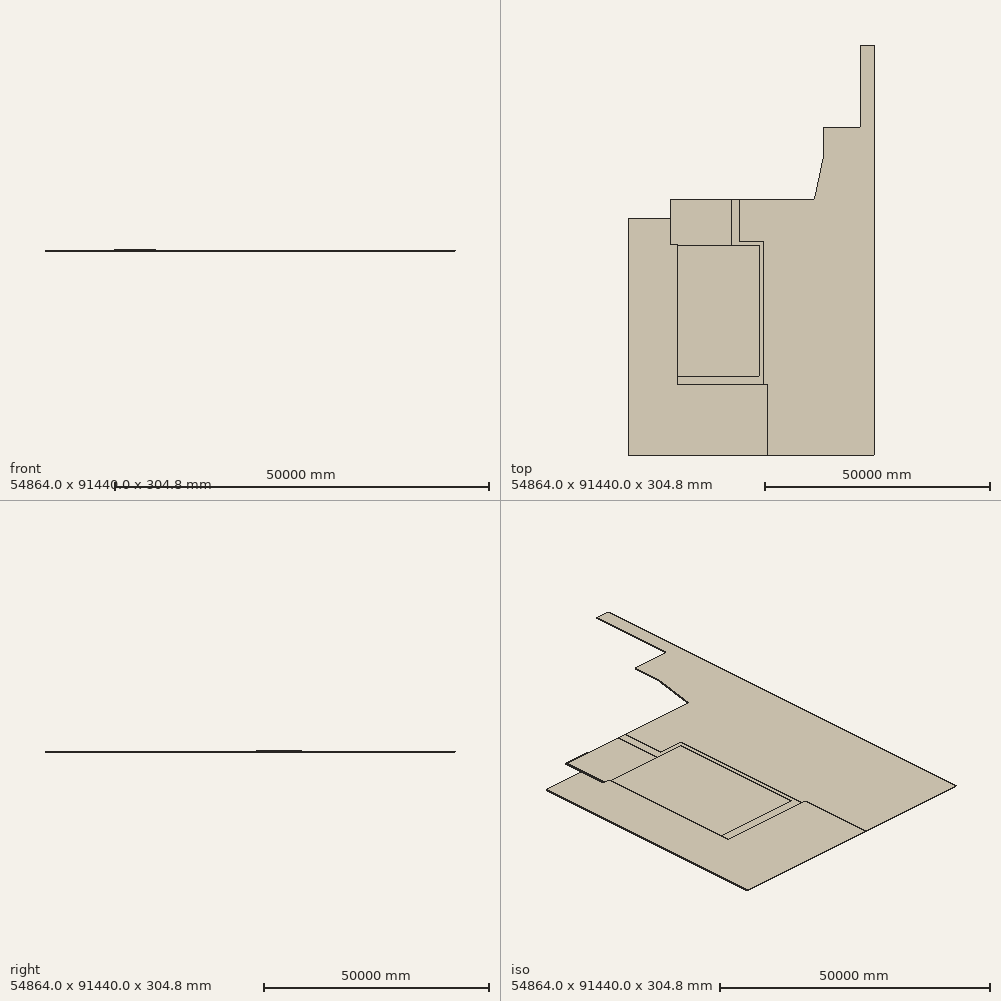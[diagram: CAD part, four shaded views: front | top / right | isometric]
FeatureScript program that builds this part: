
annotation { "Feature Type Name" : "Feature", "Feature Type Description" : "" }
export const myFeature = defineFeature(function(context is Context, id is Id, definition is map)
    precondition{}
    {
        {
            var Q0;
            Q0=qCreatedBy(makeId("Top.planeOp"),FACE);
            var sketch = newSketch(context, id + "F0", { "sketchPlane" : qUnion([Q0])});
            skLineSegment(sketch, "E0.bottom", {"start": v(0, 0) * mm, "end": v(54864, 0) * mm});
            skLineSegment(sketch, "E0.top", {"start": v(0, 91440) * mm, "end": v(54864, 91440) * mm});
            skLineSegment(sketch, "E0.left", {"start": v(0, 0) * mm, "end": v(0, 91440) * mm});
            skLineSegment(sketch, "E0.right", {"start": v(54864, 0) * mm, "end": v(54864, 91440) * mm});
            skLineSegment(sketch, "E1", {"start": v(31089.6, 0) * mm, "end": v(31089.6, 15849.6) * mm});
            skLineSegment(sketch, "E2", {"start": v(10820.4, 17678.4) * mm, "end": v(10820.4, 46786.8) * mm});
            skLineSegment(sketch, "E3", {"start": v(29260.8, 46786.8) * mm, "end": v(10820.4, 46786.8) * mm});
            skLineSegment(sketch, "E4", {"start": v(29260.8, 46786.8) * mm, "end": v(29260.8, 17678.4) * mm});
            skLineSegment(sketch, "E5", {"start": v(30175.2, 15849.6) * mm, "end": v(30175.2, 47701.2) * mm});
            skLineSegment(sketch, "E6", {"start": v(23012.4, 56997.6) * mm, "end": v(23012.4, 46786.8) * mm});
            skLineSegment(sketch, "E7", {"start": v(31089.6, 15849.6) * mm, "end": v(10820.4, 15849.6) * mm});
            skLineSegment(sketch, "E8.trimOffspring", {"start": v(29260.8, 17678.4) * mm, "end": v(10820.4, 17678.4) * mm});
            skLineSegment(sketch, "E9", {"start": v(10820.4, 15849.6) * mm, "end": v(10820.4, 17678.4) * mm});
            skLineSegment(sketch, "E10", {"start": v(10820.4, 46786.8) * mm, "end": v(10820.4, 47091.6) * mm});
            skLineSegment(sketch, "E11", {"start": v(10820.4, 47091.6) * mm, "end": v(9296.4, 47091.6) * mm});
            skLineSegment(sketch, "E12", {"start": v(9296.4, 52882.8) * mm, "end": v(0, 52882.8) * mm});
            skLineSegment(sketch, "E13", {"start": v(9296.4, 47091.6) * mm, "end": v(9296.4, 57150) * mm});
            skLineSegment(sketch, "E14", {"start": v(9296.4, 57150) * mm, "end": v(14782.8, 57150) * mm});
            skLineSegment(sketch, "E15", {"start": v(14782.8, 57150) * mm, "end": v(14782.8, 56997.6) * mm});
            skLineSegment(sketch, "E16", {"start": v(14782.8, 56997.6) * mm, "end": v(9448.8, 56997.6) * mm});
            skLineSegment(sketch, "E17", {"start": v(9448.8, 56997.6) * mm, "end": v(9448.8, 47091.6) * mm});
            skLineSegment(sketch, "E18", {"start": v(9296.4, 47091.6) * mm, "end": v(9448.8, 47091.6) * mm});
            skLineSegment(sketch, "E19", {"start": v(14782.8, 56997.6) * mm, "end": v(41452.8, 56997.6) * mm});
            skLineSegment(sketch, "E20", {"start": v(41452.8, 56997.6) * mm, "end": v(43586.4, 67056) * mm});
            skLineSegment(sketch, "E21", {"start": v(43586.4, 67056) * mm, "end": v(43586.4, 73152) * mm});
            skLineSegment(sketch, "E22", {"start": v(43586.4, 73152) * mm, "end": v(51816, 73152) * mm});
            skLineSegment(sketch, "E23", {"start": v(51816, 73152) * mm, "end": v(51816, 91440) * mm});
            skLineSegment(sketch, "E24", {"start": v(30175.2, 47701.2) * mm, "end": v(24841.2, 47701.2) * mm});
            skLineSegment(sketch, "E25", {"start": v(24841.2, 47701.2) * mm, "end": v(24841.2, 56997.6) * mm});
            skSolve(sketch);
        }
        {
            var Q0;
            {var subQ1=sQuery(id+"F0.wireOp",EDGE,"E14");Q0=makeQuery(id+"F0.imprint","IMPRINT",FACE,{"disambiguationData":[TD([[makeQuery(id+"F0.imprint","IMPRINT",EDGE,{"derivedFrom":subQ1}),-1.0]])]});}
            var Q1;
            Q1=sQuery(id+"F0.wireOp",EDGE,"E13");
            var Q2;
            Q2=sQuery(id+"F0.wireOp",EDGE,"E17");
            var Q3;
            Q3=sQuery(id+"F0.wireOp",EDGE,"E18");
            var Q4;
            Q4=sQuery(id+"F0.wireOp",EDGE,"E16");
            var Q5;
            Q5=sQuery(id+"F0.wireOp",EDGE,"E14");
            var Q6;
            Q6=sQuery(id+"F0.wireOp",EDGE,"E15");
            extrude(context, id + "F1", {"entities" : qUnion([Q0]), "surfaceEntities" : qUnion([Q1, Q2, Q3, Q4, Q5, Q6]), "depth" : 152.4 * mm});
        }
        {
            var Q0;
            {var subQ6=sQuery(id+"F0.wireOp",EDGE,"E1");Q0=makeQuery(id+"F0.imprint","IMPRINT",FACE,{"disambiguationData":[TD([[makeQuery(id+"F0.imprint","IMPRINT",EDGE,{"derivedFrom":subQ6}),1.0]])]});}
            extrude(context, id + "F2", {"entities" : qUnion([Q0]), "operationType" : NewBodyOperationType.ADD, "oppositeDirection" : true, "depth" : 152.4 * mm});
        }
        {
            var Q0;
            {var subQ3=sQuery(id+"F0.wireOp",EDGE,"E4");Q0=makeQuery(id+"F0.imprint","IMPRINT",FACE,{"disambiguationData":[TD([[makeQuery(id+"F0.imprint","IMPRINT",EDGE,{"derivedFrom":subQ3}),1.0]])]});}
            extrude(context, id + "F3", {"entities" : qUnion([Q0]), "oppositeDirection" : true, "depth" : 152.4 * mm});
        }
        {
            var Q0;
            {var subQ3=sQuery(id+"F0.wireOp",EDGE,"E2");Q0=makeQuery(id+"F0.imprint","IMPRINT",FACE,{"disambiguationData":[TD([[makeQuery(id+"F0.imprint","IMPRINT",EDGE,{"derivedFrom":subQ3}),-1.0]])]});}
            extrude(context, id + "F4", {"entities" : qUnion([Q0]), "oppositeDirection" : true, "depth" : 152.4 * mm});
        }
        {
            var Q0;
            {var subQ2=sQuery(id+"F0.wireOp",EDGE,"E6");Q0=makeQuery(id+"F0.imprint","IMPRINT",FACE,{"disambiguationData":[TD([[makeQuery(id+"F0.imprint","IMPRINT",EDGE,{"derivedFrom":subQ2}),-1.0]])]});}
            var Q1;
            {var subQ7=sQuery(id+"F0.wireOp",EDGE,"E0.right");Q1=makeQuery(id+"F0.imprint","IMPRINT",FACE,{"disambiguationData":[TD([[makeQuery(id+"F0.imprint","IMPRINT",EDGE,{"derivedFrom":subQ7}),1.0]])]});}
            extrude(context, id + "F5", {"entities" : qUnion([Q0, Q1]), "oppositeDirection" : true, "depth" : 152.4 * mm});
        }
    });
